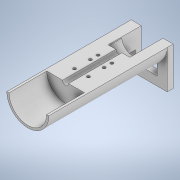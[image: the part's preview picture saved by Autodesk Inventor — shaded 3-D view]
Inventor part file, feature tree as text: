
AUTODESK INVENTOR PART (.ipt)
format: ipt  version: 2022 (Build 260153000, 153)  size: 407,040 bytes
history: native  units: mm
features: extrude x23, sketch x23, fillet x2
ambient origin geometry x8: Origin, YZ Plane, XZ Plane, XY Plane, X Axis, Y Axis, Z Axis, Center Point
bodies: Solid1 (feature_tree)
feature tree (48):
  extrude  "Extrusion1"  Depth=70.0mm
  extrude  "Extrusion2"  Depth=6.0mm TaperAngle=0.0deg
  extrude  "Extrusion3"  Depth=3.0mm
  fillet  "Fillet1"  Radius=40.0mm
  extrude  "Extrusion4"  Depth=4.0mm
  extrude  "Extrusion5"  Depth=5.0mm TaperAngle=0.0deg
  extrude  "Extrusion6"  Depth=11.0mm
  extrude  "Extrusion7"  Depth=11.0mm
  extrude  "Extrusion8"  Depth=24.0mm TaperAngle=0.0deg
  extrude  "Extrusion9"  Depth=6.0mm TaperAngle=0.0deg
  extrude  "Extrusion10"  Depth=13.8mm
  extrude  "Extrusion11"  Depth=13.8mm TaperAngle=0.0deg
  extrude  "Extrusion12"  Depth=50.0mm TaperAngle=0.0deg
  fillet  "Fillet3"  Radius=50.0mm
  extrude  "Extrusion19"  Depth=38.0mm
  extrude  "Extrusion20"  Depth=6.2mm TaperAngle=0.0deg
  extrude  "Extrusion21"  Depth=10.0mm TaperAngle=0.0deg
  extrude  "Extrusion22"  Depth=10.0mm TaperAngle=0.0deg
  extrude  "Extrusion23"  Depth=10.0mm TaperAngle=0.0deg
  extrude  "Extrusion24"  Depth=150.0mm TaperAngle=0.0deg
  extrude  "Extrusion25"  Depth=10.0mm TaperAngle=0.0deg
  extrude  "Extrusion27"  Depth=9.0mm TaperAngle=0.0deg
  extrude  "Extrusion28"  [1 undecoded]
  extrude  "Extrusion29"  [1 undecoded]
  extrude  "Extrusion30"  [1 undecoded]
  sketch  "Sketch1"  dims[d0=62.0mm d1=70.0mm]
  sketch  "Sketch2"  dims[d2=6.0mm d3=40.0mm d4=0.0mm]
  sketch  "Sketch3"  dims[d5=62.0mm d9=3.0mm d10=40.0mm d12=360.0deg]
  sketch  "Sketch4"  dims[d14=40.0mm d15=0.0mm d16=4.0mm]
  sketch  "Sketch5"  dims[d18=11.5mm d19=5.0mm d20=0.0mm]
  sketch  "Sketch6"  dims[d21=8.0mm d22=11.0mm]
  sketch  "Sketch8"  dims[d23=11.0mm d24=5.0mm]
  sketch  "Sketch9"  dims[d25=5.0mm d26=24.0mm d27=0.0mm]
  sketch  "Sketch10"  dims[d29=6.0mm d30=6.0mm d31=0.0mm]
  sketch  "Sketch11"  dims[d32=13.8mm d33=0.0mm d37=33.7mm]
  sketch  "Sketch12"  dims[d38=11.0mm d39=13.8mm d40=0.0mm]
  sketch  "Sketch13"  dims[d41=6.0mm d42=50.0mm d43=0.0mm d44=50.0mm d45=0.0mm]
  sketch  "Sketch20"  dims[d47=36.0mm d48=0.0mm d49=38.0mm]
  sketch  "Sketch21"  dims[d50=32.0mm d51=0.0mm d52=6.2mm d53=0.0mm]
  sketch  "Sketch22"  dims[d63=1.0mm d69=10.0mm d70=0.0mm]
  sketch  "Sketch23"  dims[d71=10.0mm d72=0.0mm d73=10.0mm d74=0.0mm]
  sketch  "Sketch24"  dims[d75=10.0mm d76=0.0mm d77=10.0mm d78=0.0mm]
  sketch  "Sketch25"  dims[d79=150.0mm d80=0.0mm d81=150.0mm d82=0.0mm]
  sketch  "Sketch26"  dims[d90=0.0mm d91=0.0mm d92=10.0mm d93=0.0mm]
  sketch  "Sketch28"  dims[d94=18.6mm d95=0.0mm d96=9.0mm d97=0.0mm]
  sketch  "Sketch29"
  sketch  "Sketch30"
  sketch  "Sketch31"
note: 3 required parameter values undecoded (feature->parameter linkage not recoverable at this tier; creation-order binding heuristic only, values carry confidence <= 0.55)
